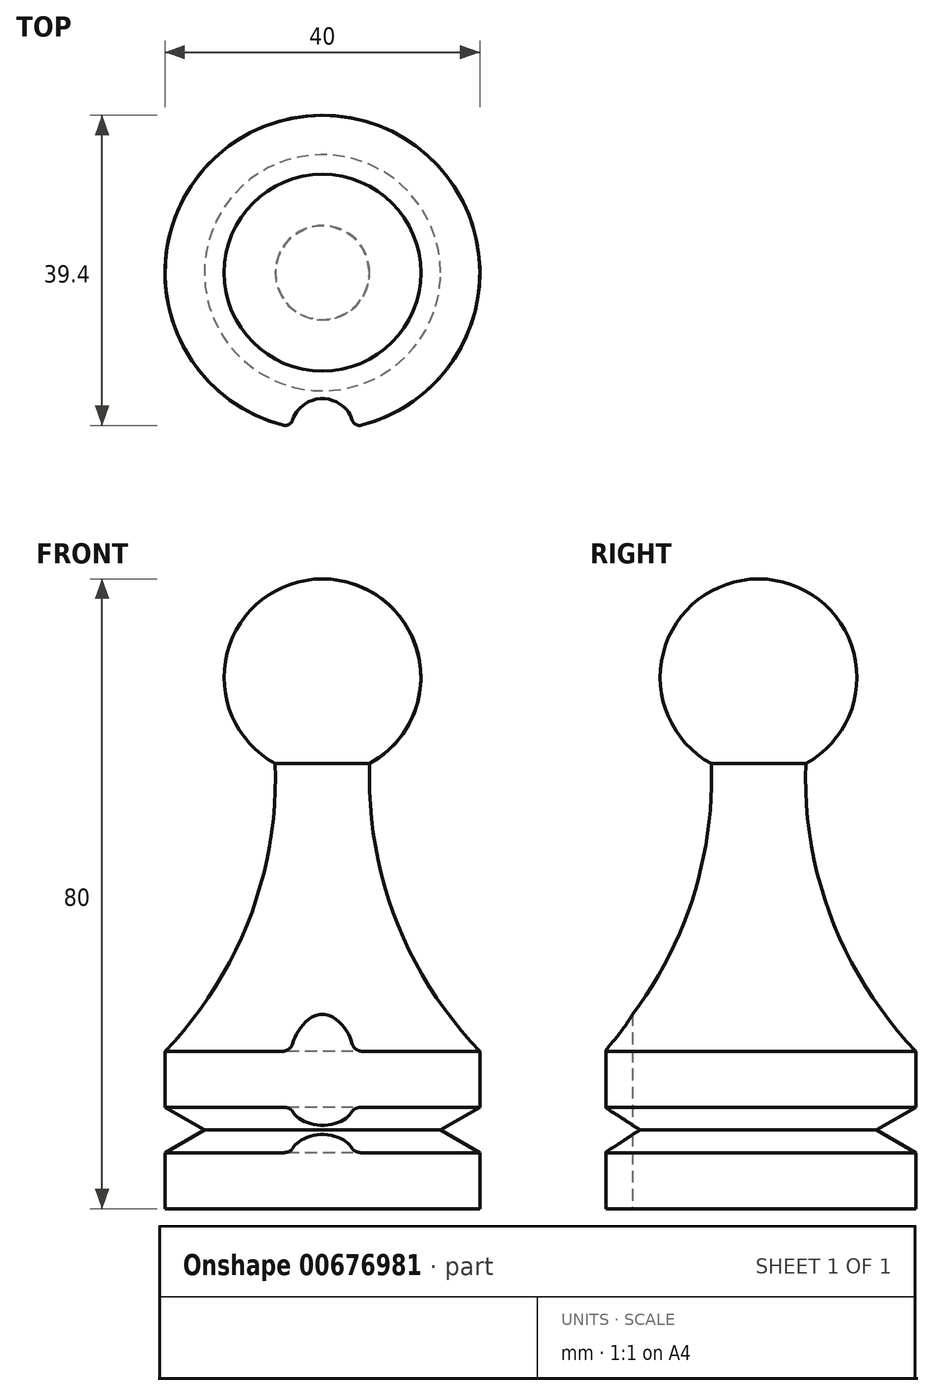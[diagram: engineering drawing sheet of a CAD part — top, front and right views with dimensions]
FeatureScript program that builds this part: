
annotation { "Feature Type Name" : "Feature", "Feature Type Description" : "" }
export const myFeature = defineFeature(function(context is Context, id is Id, definition is map)
    precondition{}
    {
        {
            var Q0;
            Q0=qCreatedBy(makeId("Front.planeOp"),FACE);
            var sketch = newSketch(context, id + "F0", { "sketchPlane" : qUnion([Q0])});
            skLineSegment(sketch, "E0", {"start": v(0, 80) * mm, "end": v(0, -41.03) * mm, "construction": true});
            skLineSegment(sketch, "E1", {"start": v(0, 0) * mm, "end": v(20, 0) * mm});
            skLineSegment(sketch, "E2", {"start": v(20, 0) * mm, "end": v(20, 7.11) * mm});
            skLineSegment(sketch, "E3", {"start": v(20, 7.11) * mm, "end": v(15, 10) * mm});
            skLineSegment(sketch, "E4", {"start": v(15, 10) * mm, "end": v(20, 12.89) * mm});
            skLineSegment(sketch, "E5", {"start": v(20, 12.89) * mm, "end": v(20, 20) * mm});
            skArc(sketch, "E6", {"start": v(6, 56.53) * mm, "mid": v(9.28, 36.84) * mm, "end": v(20, 20) * mm});
            skArc(sketch, "E7", {"start": v(6, 56.53) * mm, "mid": v(12.11, 70.6) * mm, "end": v(0, 80) * mm});
            skLineSegment(sketch, "E8", {"start": v(0, 80) * mm, "end": v(0, 0) * mm});
            skSolve(sketch);
        }
        {
            var Q0;
            Q0=makeQuery(id+"F0.imprint","IMPRINT",FACE,{"disambiguationData":[TD([[makeQuery(id+"F0.imprint","IMPRINT",EDGE,{"derivedFrom":sQuery(id+"F0.wireOp",EDGE,"E1")}),1.0]])]});
            var Q1;
            Q1=sQuery(id+"F0.wireOp",EDGE,"E0");
            revolve(context, id + "F1", {"entities" : qUnion([Q0]), "axis" : qUnion([Q1]), "revolveType" : RevolveType.FULL, "surfaceOperationType" : NewSurfaceOperationType.NEW});
        }
        {
            var Q0;
            Q0=makeQuery(id+"F1.opRevolve","SWEPT_FACE",FACE,{"disambiguationData":[OSD([sQuery(id+"F0.wireOp",EDGE,"E1")])]});
            var sketch = newSketch(context, id + "F2", { "sketchPlane" : qUnion([Q0])});
            skCircle(sketch, "E9", {"center": v(0, 20) * mm, "radius": 4 * mm});
            skSolve(sketch);
        }
        {
            var Q0;
            {var subQ0=sQuery(id+"F2.wireOp",EDGE,"E9");var subQ1=makeQuery(id+"F1.opRevolve","SWEPT_EDGE",EDGE,{"disambiguationData":[OSD([sQuery(id+"F0.wireOp",EDGE,"E1"),sQuery(id+"F0.wireOp",EDGE,"E2")])]});var subQ2=makeQuery(id+"F2.imprint","INTERSECT",VERTEX,{"disambiguationData":[OD(0.0)],"derivedFrom":[subQ1,subQ0]});Q0=makeQuery(id+"F2.imprint","IMPRINT",FACE,{"disambiguationData":[TD([[makeQuery(id+"F2.imprint","IMPRINT",EDGE,{"disambiguationData":[TD([[subQ2,-1.0]])],"derivedFrom":subQ0}),1.0]])]});}
            var Q1;
            {var subQ0=sQuery(id+"F2.wireOp",EDGE,"E9");var subQ1=makeQuery(id+"F1.opRevolve","SWEPT_EDGE",EDGE,{"disambiguationData":[OSD([sQuery(id+"F0.wireOp",EDGE,"E1"),sQuery(id+"F0.wireOp",EDGE,"E2")])]});var subQ2=makeQuery(id+"F2.imprint","INTERSECT",VERTEX,{"disambiguationData":[OD(0.0)],"derivedFrom":[subQ1,subQ0]});Q1=makeQuery(id+"F2.imprint","IMPRINT",FACE,{"disambiguationData":[TD([[makeQuery(id+"F2.imprint","IMPRINT",EDGE,{"disambiguationData":[TD([[subQ2,1.0]])],"derivedFrom":subQ0}),1.0]])]});}
            extrude(context, id + "F3", {"entities" : qUnion([Q0, Q1]), "operationType" : NewBodyOperationType.REMOVE, "oppositeDirection" : true, "depth" : 30.6 * mm, "offsetDistance" : 25 * mm});
        }
        {
            var Q0;
            Q0=makeQuery(id+"F3.boolean.opBoolean","INTERSECT",EDGE,{"disambiguationData":[OD(0.0)],"derivedFrom":[makeQuery(id+"F1.opRevolve","SWEPT_FACE",FACE,{"disambiguationData":[OSD([sQuery(id+"F0.wireOp",EDGE,"E5")])]}),makeQuery(id+"F3.opExtrude","SWEPT_FACE",FACE,{"disambiguationData":[OSD([sQuery(id+"F2.wireOp",EDGE,"E9")])]})]});
            var Q1;
            Q1=makeQuery(id+"F3.boolean.opBoolean","INTERSECT",EDGE,{"disambiguationData":[OD(1.0)],"derivedFrom":[makeQuery(id+"F1.opRevolve","SWEPT_FACE",FACE,{"disambiguationData":[OSD([sQuery(id+"F0.wireOp",EDGE,"E5")])]}),makeQuery(id+"F3.opExtrude","SWEPT_FACE",FACE,{"disambiguationData":[OSD([sQuery(id+"F2.wireOp",EDGE,"E9")])]})]});
            var Q2;
            Q2=makeQuery(id+"F3.boolean.opBoolean","INTERSECT",EDGE,{"disambiguationData":[OD(0.0)],"derivedFrom":[makeQuery(id+"F1.opRevolve","SWEPT_FACE",FACE,{"disambiguationData":[OSD([sQuery(id+"F0.wireOp",EDGE,"E2")])]}),makeQuery(id+"F3.opExtrude","SWEPT_FACE",FACE,{"disambiguationData":[OSD([sQuery(id+"F2.wireOp",EDGE,"E9")])]})]});
            var Q3;
            Q3=makeQuery(id+"F3.boolean.opBoolean","INTERSECT",EDGE,{"disambiguationData":[OD(1.0)],"derivedFrom":[makeQuery(id+"F1.opRevolve","SWEPT_FACE",FACE,{"disambiguationData":[OSD([sQuery(id+"F0.wireOp",EDGE,"E2")])]}),makeQuery(id+"F3.opExtrude","SWEPT_FACE",FACE,{"disambiguationData":[OSD([sQuery(id+"F2.wireOp",EDGE,"E9")])]})]});
            fillet(context, id + "F4", {"entities" : qUnion([Q0, Q1, Q2, Q3]), "radius" : 1 * mm, "tangentPropagation" : true, "allowEdgeOverflow" : false});
        }
    });
